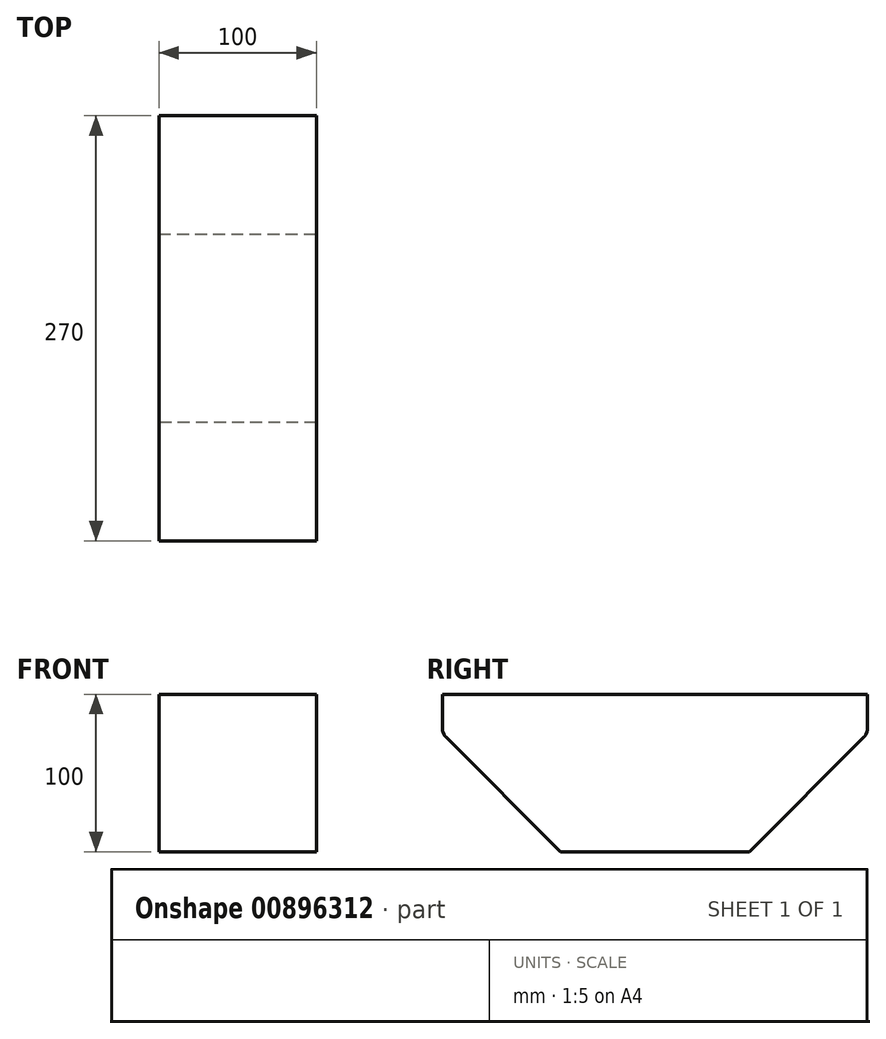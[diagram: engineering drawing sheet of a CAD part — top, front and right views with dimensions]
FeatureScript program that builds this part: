
annotation { "Feature Type Name" : "Feature", "Feature Type Description" : "" }
export const myFeature = defineFeature(function(context is Context, id is Id, definition is map)
    precondition{}
    {
        {
            var Q0;
            Q0=qCreatedBy(makeId("Top.planeOp"),FACE);
            var sketch = newSketch(context, id + "F0", { "sketchPlane" : qUnion([Q0])});
            skLineSegment(sketch, "E0.bottom", {"start": v(-50, 135) * mm, "end": v(50, 135) * mm});
            skLineSegment(sketch, "E0.top", {"start": v(-50, -135) * mm, "end": v(50, -135) * mm});
            skLineSegment(sketch, "E0.left", {"start": v(-50, 135) * mm, "end": v(-50, -135) * mm});
            skLineSegment(sketch, "E0.right", {"start": v(50, 135) * mm, "end": v(50, -135) * mm});
            skPoint(sketch, "E0.middle", {"position": v(0, 0) * mm});
            skSolve(sketch);
        }
        {
            var Q0;
            Q0=makeQuery(id+"F0.imprint","IMPRINT",FACE,{"disambiguationData":[TD([[makeQuery(id+"F0.imprint","IMPRINT",EDGE,{"derivedFrom":sQuery(id+"F0.wireOp",EDGE,"E0.bottom")}),-1.0]])]});
            extrude(context, id + "F1", {"entities" : qUnion([Q0]), "depth" : 100 * mm, "offsetDistance" : 25 * mm});
        }
        {
            var Q0;
            Q0=makeQuery(id+"F1.opExtrude","CAP_EDGE",EDGE,{"disambiguationData":[OSD([sQuery(id+"F0.wireOp",EDGE,"E0.top")])],"isStart":true});
            var Q1;
            Q1=makeQuery(id+"F1.opExtrude","CAP_EDGE",EDGE,{"disambiguationData":[OSD([sQuery(id+"F0.wireOp",EDGE,"E0.bottom")])],"isStart":true});
            chamfer(context, id + "F2", {"entities" : qUnion([Q0, Q1]), "width" : 75 * mm, "tangentPropagation" : true});
        }
        {
            var Q0;
            {var subQ0=sQuery(id+"F0.wireOp",EDGE,"E0.top");Q0=makeQuery(id+"F2.opChamfer","BLEND_EDGE",EDGE,{"blendedFrom":[makeQuery(id+"F1.opExtrude","CAP_EDGE",EDGE,{"disambiguationData":[OSD([subQ0])],"isStart":true}),makeQuery(id+"F1.opExtrude","SWEPT_FACE",FACE,{"disambiguationData":[OSD([subQ0])]})],"blendedInto":[makeQuery(id+"F1.opExtrude","SWEPT_FACE",FACE,{"disambiguationData":[OSD([subQ0])]})]});}
            var Q1;
            {var subQ0=sQuery(id+"F0.wireOp",EDGE,"E0.bottom");Q1=makeQuery(id+"F2.opChamfer","BLEND_EDGE",EDGE,{"blendedFrom":[makeQuery(id+"F1.opExtrude","CAP_EDGE",EDGE,{"disambiguationData":[OSD([subQ0])],"isStart":true}),makeQuery(id+"F1.opExtrude","SWEPT_FACE",FACE,{"disambiguationData":[OSD([subQ0])]})],"blendedInto":[makeQuery(id+"F1.opExtrude","SWEPT_FACE",FACE,{"disambiguationData":[OSD([subQ0])]})]});}
            chamfer(context, id + "F3", {"entities" : qUnion([Q0, Q1]), "width" : 5 * mm, "tangentPropagation" : true});
        }
        {
            var Q0;
            {var subQ0=sQuery(id+"F0.wireOp",EDGE,"E0.bottom");var subQ1=makeQuery(id+"F1.opExtrude","SWEPT_FACE",FACE,{"disambiguationData":[OSD([subQ0])]});Q0=makeQuery(id+"F3.opChamfer","BLEND_EDGE",EDGE,{"blendedFrom":[makeQuery(id+"F2.opChamfer","BLEND_EDGE",EDGE,{"blendedFrom":[makeQuery(id+"F1.opExtrude","CAP_EDGE",EDGE,{"disambiguationData":[OSD([subQ0])],"isStart":true}),subQ1],"blendedInto":[subQ1]}),subQ1],"blendedInto":[subQ1]});}
            var Q1;
            {var subQ0=sQuery(id+"F0.wireOp",EDGE,"E0.bottom");Q1=makeQuery(id+"F3.opChamfer","BLEND_EDGE",EDGE,{"blendedFrom":[makeQuery(id+"F2.opChamfer","BLEND_EDGE",EDGE,{"blendedFrom":[makeQuery(id+"F1.opExtrude","CAP_EDGE",EDGE,{"disambiguationData":[OSD([subQ0])],"isStart":true}),makeQuery(id+"F1.opExtrude","SWEPT_FACE",FACE,{"disambiguationData":[OSD([subQ0])]})],"blendedInto":[makeQuery(id+"F1.opExtrude","SWEPT_FACE",FACE,{"disambiguationData":[OSD([subQ0])]})]}),makeQuery(id+"F2.opChamfer","BLEND_FACE",FACE,{"disambiguationData":[OSD([subQ0])]})],"blendedInto":[makeQuery(id+"F2.opChamfer","BLEND_FACE",FACE,{"disambiguationData":[OSD([subQ0])]})]});}
            var Q2;
            {var subQ0=sQuery(id+"F0.wireOp",EDGE,"E0.top");var subQ1=makeQuery(id+"F1.opExtrude","SWEPT_FACE",FACE,{"disambiguationData":[OSD([subQ0])]});Q2=makeQuery(id+"F3.opChamfer","BLEND_EDGE",EDGE,{"blendedFrom":[makeQuery(id+"F2.opChamfer","BLEND_EDGE",EDGE,{"blendedFrom":[makeQuery(id+"F1.opExtrude","CAP_EDGE",EDGE,{"disambiguationData":[OSD([subQ0])],"isStart":true}),subQ1],"blendedInto":[subQ1]}),subQ1],"blendedInto":[subQ1]});}
            var Q3;
            {var subQ0=sQuery(id+"F0.wireOp",EDGE,"E0.top");Q3=makeQuery(id+"F3.opChamfer","BLEND_EDGE",EDGE,{"blendedFrom":[makeQuery(id+"F2.opChamfer","BLEND_EDGE",EDGE,{"blendedFrom":[makeQuery(id+"F1.opExtrude","CAP_EDGE",EDGE,{"disambiguationData":[OSD([subQ0])],"isStart":true}),makeQuery(id+"F1.opExtrude","SWEPT_FACE",FACE,{"disambiguationData":[OSD([subQ0])]})],"blendedInto":[makeQuery(id+"F1.opExtrude","SWEPT_FACE",FACE,{"disambiguationData":[OSD([subQ0])]})]}),makeQuery(id+"F2.opChamfer","BLEND_FACE",FACE,{"disambiguationData":[OSD([subQ0])]})],"blendedInto":[makeQuery(id+"F2.opChamfer","BLEND_FACE",FACE,{"disambiguationData":[OSD([subQ0])]})]});}
            fillet(context, id + "F4", {"entities" : qUnion([Q0, Q1, Q2, Q3]), "radius" : 5 * mm, "tangentPropagation" : true, "allowEdgeOverflow" : false});
        }
    });
